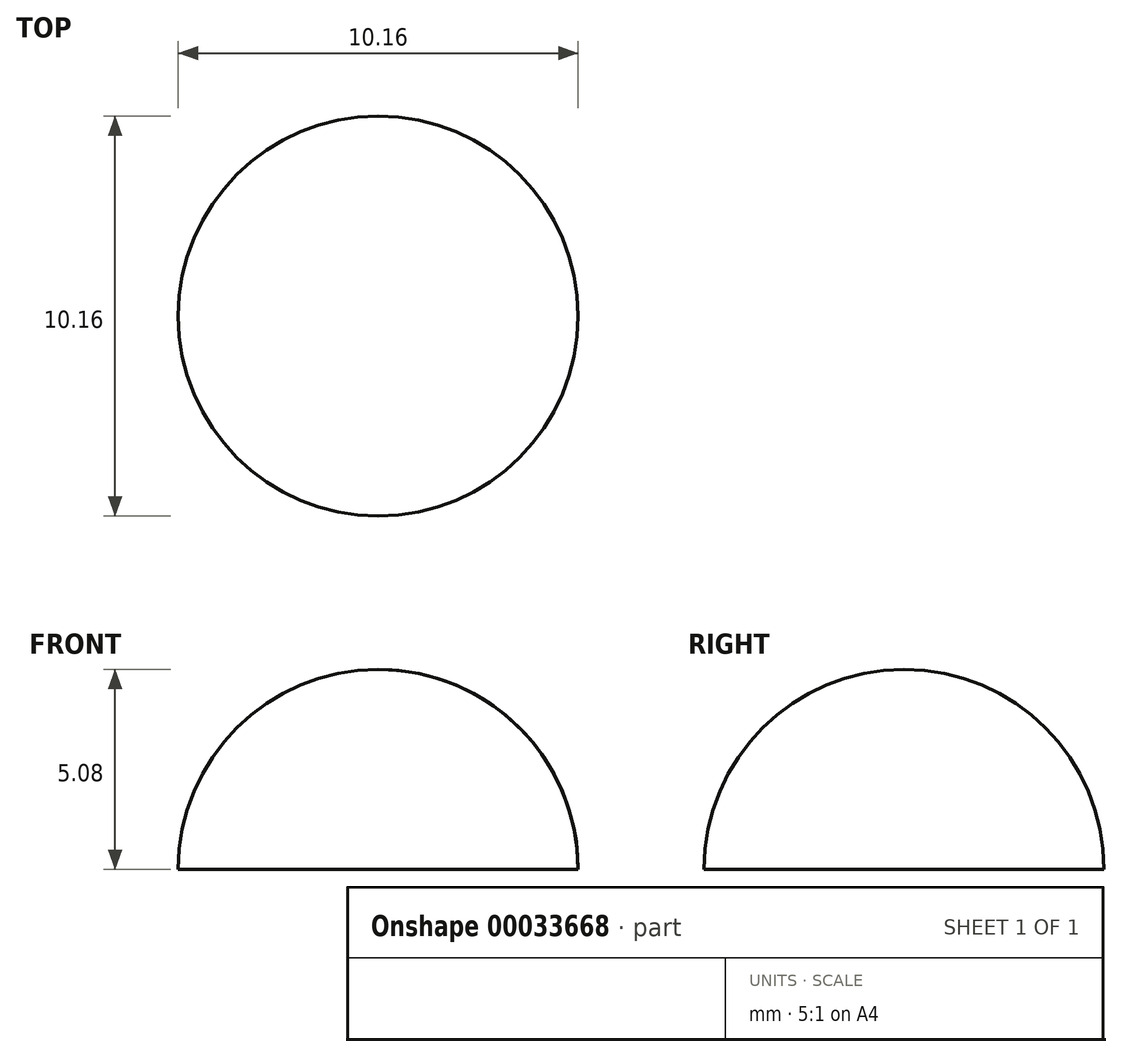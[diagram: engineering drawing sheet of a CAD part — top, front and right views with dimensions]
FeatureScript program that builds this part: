
annotation { "Feature Type Name" : "Feature", "Feature Type Description" : "" }
export const myFeature = defineFeature(function(context is Context, id is Id, definition is map)
    precondition{}
    {
        {
            var Q0;
            Q0=qCreatedBy(makeId("Front.planeOp"),FACE);
            var sketch = newSketch(context, id + "F0", { "sketchPlane" : qUnion([Q0])});
            skLineSegment(sketch, "E0", {"start": v(-1.2, 13.63) * mm, "end": v(-1.2, -15.75) * mm, "construction": true});
            skArc(sketch, "E1", {"start": v(3.88, -1.18) * mm, "mid": v(2.4, 2.41) * mm, "end": v(-1.2, 3.9) * mm});
            skLineSegment(sketch, "E2", {"start": v(-8.64, -1.18) * mm, "end": v(6.7, -1.18) * mm});
            skLineSegment(sketch, "E3", {"start": v(-1.2, 3.9) * mm, "end": v(-1.2, -1.18) * mm});
            skLineSegment(sketch, "E4", {"start": v(3.88, -1.18) * mm, "end": v(-1.2, -1.18) * mm});
            skSolve(sketch);
        }
        {
            var Q0;
            Q0=makeQuery(id+"F0.imprint","IMPRINT",FACE,{"disambiguationData":[TD([[makeQuery(id+"F0.imprint","IMPRINT",EDGE,{"derivedFrom":sQuery(id+"F0.wireOp",EDGE,"E1")}),1.0]])]});
            var Q1;
            Q1=sQuery(id+"F0.wireOp",EDGE,"E0");
            revolve(context, id + "F1", {"entities" : qUnion([Q0]), "axis" : qUnion([Q1]), "revolveType" : RevolveType.FULL});
        }
    });
